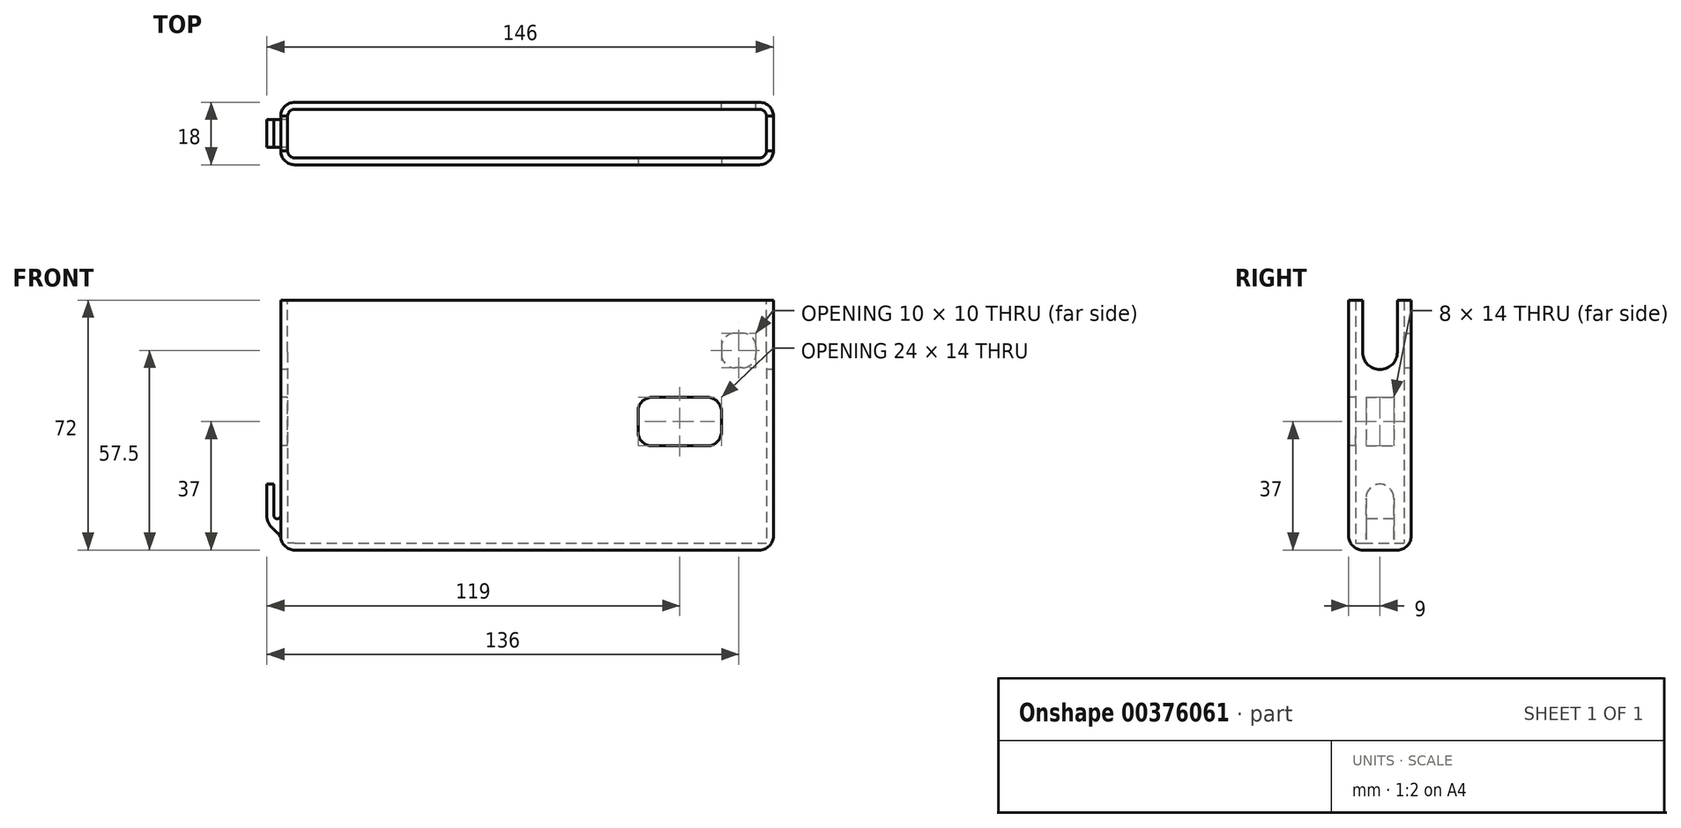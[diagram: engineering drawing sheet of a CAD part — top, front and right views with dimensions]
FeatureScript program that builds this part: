
annotation { "Feature Type Name" : "Feature", "Feature Type Description" : "" }
export const myFeature = defineFeature(function(context is Context, id is Id, definition is map)
    precondition{}
    {
        {
            var Q0;
            Q0=qCreatedBy(makeId("Top.planeOp"),FACE);
            var sketch = newSketch(context, id + "F0", { "sketchPlane" : qUnion([Q0])});
            skLineSegment(sketch, "E0.bottom", {"start": v(0, 0) * mm, "end": v(142, 0) * mm});
            skLineSegment(sketch, "E0.top", {"start": v(0, 18) * mm, "end": v(142, 18) * mm});
            skLineSegment(sketch, "E0.left", {"start": v(0, 0) * mm, "end": v(0, 18) * mm});
            skLineSegment(sketch, "E0.right", {"start": v(142, 0) * mm, "end": v(142, 18) * mm});
            skSolve(sketch);
        }
        {
            var Q0;
            Q0=qSketchRegion(id+"F0",true);
            extrude(context, id + "F1", {"entities" : qUnion([Q0]), "depth" : 2 * mm});
        }
        {
            var Q0;
            Q0=makeQuery(id+"F1.opExtrude","CAP_FACE",FACE,{"disambiguationData":[OSD([sQuery(id+"F0.wireOp",EDGE,"E0.bottom"),sQuery(id+"F0.wireOp",EDGE,"E0.top"),sQuery(id+"F0.wireOp",EDGE,"E0.left"),sQuery(id+"F0.wireOp",EDGE,"E0.right")])],"isStart":false});
            var sketch = newSketch(context, id + "F2", { "sketchPlane" : qUnion([Q0])});
            skLineSegment(sketch, "E1.0", {"start": v(0, 18) * mm, "end": v(142, 18) * mm});
            skLineSegment(sketch, "E1.1", {"start": v(0, 0) * mm, "end": v(0, 18) * mm});
            skLineSegment(sketch, "E1.2", {"start": v(0, 0) * mm, "end": v(142, 0) * mm});
            skLineSegment(sketch, "E1.3", {"start": v(142, 0) * mm, "end": v(142, 18) * mm});
            skLineSegment(sketch, "E2.0", {"start": v(2, 16) * mm, "end": v(140, 16) * mm});
            skLineSegment(sketch, "E2.1", {"start": v(2, 2) * mm, "end": v(2, 16) * mm});
            skLineSegment(sketch, "E2.2", {"start": v(2, 2) * mm, "end": v(140, 2) * mm});
            skLineSegment(sketch, "E2.3", {"start": v(140, 2) * mm, "end": v(140, 16) * mm});
            skSolve(sketch);
        }
        {
            var Q0;
            Q0=qSketchRegion(id+"F2",true);
            extrude(context, id + "F3", {"entities" : qUnion([Q0]), "operationType" : NewBodyOperationType.ADD, "depth" : 70 * mm});
        }
        {
            var Q0;
            Q0=makeQuery(id+"F3.opExtrude","SWEPT_EDGE",EDGE,{"disambiguationData":[OSD([sQuery(id+"F2.wireOp",EDGE,"E2.1"),sQuery(id+"F2.wireOp",EDGE,"E2.2")])]});
            var Q1;
            Q1=makeQuery(id+"F3.opExtrude","SWEPT_EDGE",EDGE,{"disambiguationData":[OSD([sQuery(id+"F2.wireOp",EDGE,"E2.0"),sQuery(id+"F2.wireOp",EDGE,"E2.1")])]});
            var Q2;
            Q2=makeQuery(id+"F3.opExtrude","SWEPT_EDGE",EDGE,{"disambiguationData":[OSD([sQuery(id+"F2.wireOp",EDGE,"E2.0"),sQuery(id+"F2.wireOp",EDGE,"E2.3")])]});
            var Q3;
            Q3=makeQuery(id+"F3.opExtrude","SWEPT_EDGE",EDGE,{"disambiguationData":[OSD([sQuery(id+"F2.wireOp",EDGE,"E2.2"),sQuery(id+"F2.wireOp",EDGE,"E2.3")])]});
            var Q4;
            Q4=makeQuery(id+"F3.opExtrude","CAP_EDGE",EDGE,{"disambiguationData":[OSD([sQuery(id+"F2.wireOp",EDGE,"E2.2")])],"isStart":true});
            var Q5;
            Q5=makeQuery(id+"F3.opExtrude","CAP_EDGE",EDGE,{"disambiguationData":[OSD([sQuery(id+"F2.wireOp",EDGE,"E2.3")])],"isStart":true});
            var Q6;
            Q6=makeQuery(id+"F3.opExtrude","CAP_EDGE",EDGE,{"disambiguationData":[OSD([sQuery(id+"F2.wireOp",EDGE,"E2.0")])],"isStart":true});
            var Q7;
            Q7=makeQuery(id+"F3.opExtrude","CAP_EDGE",EDGE,{"disambiguationData":[OSD([sQuery(id+"F2.wireOp",EDGE,"E2.1")])],"isStart":true});
            fillet(context, id + "F4", {"entities" : qUnion([Q0, Q1, Q2, Q3, Q4, Q5, Q6, Q7]), "radius" : 2 * mm, "tangentPropagation" : true, "allowEdgeOverflow" : false});
        }
        {
            var Q0;
            Q0=makeQuery(id+"F3.boolean.opBoolean","MERGE",EDGE,{"derivedFrom":[makeQuery(id+"F1.opExtrude","SWEPT_EDGE",EDGE,{"disambiguationData":[OSD([sQuery(id+"F0.wireOp",EDGE,"E0.bottom"),sQuery(id+"F0.wireOp",EDGE,"E0.left")])]}),makeQuery(id+"F3.opExtrude","SWEPT_EDGE",EDGE,{"disambiguationData":[OSD([sQuery(id+"F2.wireOp",EDGE,"E1.1"),sQuery(id+"F2.wireOp",EDGE,"E1.2")])]})]});
            var Q1;
            Q1=makeQuery(id+"F3.boolean.opBoolean","MERGE",EDGE,{"derivedFrom":[makeQuery(id+"F1.opExtrude","SWEPT_EDGE",EDGE,{"disambiguationData":[OSD([sQuery(id+"F0.wireOp",EDGE,"E0.top"),sQuery(id+"F0.wireOp",EDGE,"E0.left")])]}),makeQuery(id+"F3.opExtrude","SWEPT_EDGE",EDGE,{"disambiguationData":[OSD([sQuery(id+"F2.wireOp",EDGE,"E1.0"),sQuery(id+"F2.wireOp",EDGE,"E1.1")])]})]});
            var Q2;
            Q2=makeQuery(id+"F3.boolean.opBoolean","MERGE",EDGE,{"derivedFrom":[makeQuery(id+"F1.opExtrude","SWEPT_EDGE",EDGE,{"disambiguationData":[OSD([sQuery(id+"F0.wireOp",EDGE,"E0.top"),sQuery(id+"F0.wireOp",EDGE,"E0.right")])]}),makeQuery(id+"F3.opExtrude","SWEPT_EDGE",EDGE,{"disambiguationData":[OSD([sQuery(id+"F2.wireOp",EDGE,"E1.0"),sQuery(id+"F2.wireOp",EDGE,"E1.3")])]})]});
            var Q3;
            Q3=makeQuery(id+"F3.boolean.opBoolean","MERGE",EDGE,{"derivedFrom":[makeQuery(id+"F1.opExtrude","SWEPT_EDGE",EDGE,{"disambiguationData":[OSD([sQuery(id+"F0.wireOp",EDGE,"E0.bottom"),sQuery(id+"F0.wireOp",EDGE,"E0.right")])]}),makeQuery(id+"F3.opExtrude","SWEPT_EDGE",EDGE,{"disambiguationData":[OSD([sQuery(id+"F2.wireOp",EDGE,"E1.2"),sQuery(id+"F2.wireOp",EDGE,"E1.3")])]})]});
            var Q4;
            Q4=makeQuery(id+"F1.opExtrude","CAP_EDGE",EDGE,{"disambiguationData":[OSD([sQuery(id+"F0.wireOp",EDGE,"E0.bottom")])],"isStart":true});
            var Q5;
            Q5=makeQuery(id+"F1.opExtrude","CAP_EDGE",EDGE,{"disambiguationData":[OSD([sQuery(id+"F0.wireOp",EDGE,"E0.left")])],"isStart":true});
            var Q6;
            Q6=makeQuery(id+"F1.opExtrude","CAP_EDGE",EDGE,{"disambiguationData":[OSD([sQuery(id+"F0.wireOp",EDGE,"E0.top")])],"isStart":true});
            var Q7;
            Q7=makeQuery(id+"F1.opExtrude","CAP_EDGE",EDGE,{"disambiguationData":[OSD([sQuery(id+"F0.wireOp",EDGE,"E0.right")])],"isStart":true});
            fillet(context, id + "F5", {"entities" : qUnion([Q0, Q1, Q2, Q3, Q4, Q5, Q6, Q7]), "radius" : 4 * mm, "tangentPropagation" : true, "allowEdgeOverflow" : false});
        }
        {
            var Q0;
            Q0=makeQuery(id+"F3.boolean.opBoolean","MERGE",FACE,{"derivedFrom":[makeQuery(id+"F1.opExtrude","SWEPT_FACE",FACE,{"disambiguationData":[OSD([sQuery(id+"F0.wireOp",EDGE,"E0.left")])]}),makeQuery(id+"F3.opExtrude","SWEPT_FACE",FACE,{"disambiguationData":[OSD([sQuery(id+"F2.wireOp",EDGE,"E1.1")])]})]});
            var sketch = newSketch(context, id + "F6", { "sketchPlane" : qUnion([Q0])});
            skLineSegment(sketch, "E3", {"start": v(-9, 72) * mm, "end": v(-9, 57) * mm, "construction": true});
            skArc(sketch, "E4.0.startCap", {"start": v(-14, 72) * mm, "mid": v(-9, 77) * mm, "end": v(-4, 72) * mm});
            skArc(sketch, "E4.0.endCap", {"start": v(-4, 57) * mm, "mid": v(-9, 52) * mm, "end": v(-14, 57) * mm});
            skLineSegment(sketch, "E4.0.left", {"start": v(-4, 72) * mm, "end": v(-4, 57) * mm});
            skLineSegment(sketch, "E4.0.right", {"start": v(-14, 72) * mm, "end": v(-14, 57) * mm});
            skSolve(sketch);
        }
        {
            var Q0;
            Q0=qSketchRegion(id+"F6",true);
            extrude(context, id + "F7", {"entities" : qUnion([Q0]), "operationType" : NewBodyOperationType.REMOVE, "endBound" : BoundingType.THROUGH_ALL, "oppositeDirection" : true, "depth" : 25 * mm});
        }
        {
            var Q0;
            Q0=makeQuery(id+"F3.boolean.opBoolean","MERGE",FACE,{"derivedFrom":[makeQuery(id+"F1.opExtrude","SWEPT_FACE",FACE,{"disambiguationData":[OSD([sQuery(id+"F0.wireOp",EDGE,"E0.bottom")])]}),makeQuery(id+"F3.opExtrude","SWEPT_FACE",FACE,{"disambiguationData":[OSD([sQuery(id+"F2.wireOp",EDGE,"E1.2")])]})]});
            var sketch = newSketch(context, id + "F8", { "sketchPlane" : qUnion([Q0])});
            skLineSegment(sketch, "E5.bottom", {"start": v(107, 44) * mm, "end": v(123, 44) * mm});
            skLineSegment(sketch, "E5.top", {"start": v(107, 30) * mm, "end": v(123, 30) * mm});
            skLineSegment(sketch, "E5.left", {"start": v(103, 40) * mm, "end": v(103, 34) * mm});
            skLineSegment(sketch, "E5.right", {"start": v(127, 40) * mm, "end": v(127, 34) * mm});
            skPoint(sketch, "E6", {"position": v(103, 37) * mm});
            skPoint(sketch, "E7.visualSharp", {"position": v(103, 44) * mm});
            skArc(sketch, "E7.filletArc", {"start": v(107, 44) * mm, "mid": v(104.17, 42.83) * mm, "end": v(103, 40) * mm});
            skPoint(sketch, "E8.visualSharp", {"position": v(127, 44) * mm});
            skArc(sketch, "E8.filletArc", {"start": v(127, 40) * mm, "mid": v(125.83, 42.83) * mm, "end": v(123, 44) * mm});
            skPoint(sketch, "E9.visualSharp", {"position": v(127, 30) * mm});
            skArc(sketch, "E9.filletArc", {"start": v(123, 30) * mm, "mid": v(125.83, 31.17) * mm, "end": v(127, 34) * mm});
            skPoint(sketch, "E10.visualSharp", {"position": v(103, 30) * mm});
            skArc(sketch, "E10.filletArc", {"start": v(103, 34) * mm, "mid": v(104.17, 31.17) * mm, "end": v(107, 30) * mm});
            skPoint(sketch, "E11", {"position": v(115, 44) * mm});
            skSolve(sketch);
        }
        {
            var Q0;
            Q0=qSketchRegion(id+"F8",true);
            extrude(context, id + "F9", {"entities" : qUnion([Q0]), "operationType" : NewBodyOperationType.REMOVE, "endBound" : BoundingType.UP_TO_NEXT, "oppositeDirection" : true, "depth" : 25 * mm});
        }
        {
            var Q0;
            Q0=makeQuery(id+"F3.boolean.opBoolean","MERGE",FACE,{"derivedFrom":[makeQuery(id+"F1.opExtrude","SWEPT_FACE",FACE,{"disambiguationData":[OSD([sQuery(id+"F0.wireOp",EDGE,"E0.left")])]}),makeQuery(id+"F3.opExtrude","SWEPT_FACE",FACE,{"disambiguationData":[OSD([sQuery(id+"F2.wireOp",EDGE,"E1.1")])]})]});
            var sketch = newSketch(context, id + "F10", { "sketchPlane" : qUnion([Q0])});
            skLineSegment(sketch, "E12.bottom", {"start": v(-13, 19) * mm, "end": v(-5, 19) * mm});
            skLineSegment(sketch, "E12.top", {"start": v(-13, 4) * mm, "end": v(-5, 4) * mm});
            skLineSegment(sketch, "E12.left", {"start": v(-13, 19) * mm, "end": v(-13, 4) * mm});
            skLineSegment(sketch, "E12.right", {"start": v(-5, 19) * mm, "end": v(-5, 4) * mm});
            skPoint(sketch, "E13", {"position": v(-9, 4) * mm});
            skSolve(sketch);
        }
        {
            var Q0;
            Q0=qSketchRegion(id+"F10",true);
            extrude(context, id + "F11", {"entities" : qUnion([Q0]), "operationType" : NewBodyOperationType.ADD, "depth" : 4 * mm});
        }
        {
            var Q0;
            Q0=makeQuery(id+"F11.opExtrude","CAP_EDGE",EDGE,{"disambiguationData":[OSD([sQuery(id+"F10.wireOp",EDGE,"E12.top")])],"isStart":false});
            chamfer(context, id + "F12", {"entities" : qUnion([Q0]), "width" : 4 * mm, "tangentPropagation" : true});
        }
        {
            var Q0;
            Q0=makeQuery(id+"F11.opExtrude","SWEPT_FACE",FACE,{"disambiguationData":[OSD([sQuery(id+"F10.wireOp",EDGE,"E12.bottom")])]});
            var sketch = newSketch(context, id + "F13", { "sketchPlane" : qUnion([Q0])});
            skLineSegment(sketch, "E14.bottom", {"start": v(-2, 13) * mm, "end": v(0, 13) * mm});
            skLineSegment(sketch, "E14.top", {"start": v(-2, 5) * mm, "end": v(0, 5) * mm});
            skLineSegment(sketch, "E14.left", {"start": v(0, 5) * mm, "end": v(0, 13) * mm});
            skLineSegment(sketch, "E14.right", {"start": v(-2, 5) * mm, "end": v(-2, 13) * mm});
            skSolve(sketch);
        }
        {
            var Q0;
            Q0=qSketchRegion(id+"F13",true);
            extrude(context, id + "F14", {"entities" : qUnion([Q0]), "operationType" : NewBodyOperationType.REMOVE, "oppositeDirection" : true, "depth" : 10 * mm});
        }
        {
            var Q0;
            Q0=makeQuery(id+"F11.opExtrude","SWEPT_EDGE",EDGE,{"disambiguationData":[OSD([sQuery(id+"F10.wireOp",EDGE,"E12.bottom"),sQuery(id+"F10.wireOp",EDGE,"E12.left")])]});
            var Q1;
            Q1=makeQuery(id+"F11.opExtrude","SWEPT_EDGE",EDGE,{"disambiguationData":[OSD([sQuery(id+"F10.wireOp",EDGE,"E12.bottom"),sQuery(id+"F10.wireOp",EDGE,"E12.right")])]});
            var Q2;
            {var subQ0=sQuery(id+"F10.wireOp",EDGE,"E12.top");Q2=makeQuery(id+"F12.opChamfer","BLEND_EDGE",EDGE,{"blendedFrom":[makeQuery(id+"F11.opExtrude","CAP_EDGE",EDGE,{"disambiguationData":[OSD([subQ0])],"isStart":false}),makeQuery(id+"F11.opExtrude","CAP_FACE",FACE,{"disambiguationData":[OSD([sQuery(id+"F10.wireOp",EDGE,"E12.bottom"),subQ0,sQuery(id+"F10.wireOp",EDGE,"E12.left"),sQuery(id+"F10.wireOp",EDGE,"E12.right")])],"isStart":false})],"blendedInto":[makeQuery(id+"F11.opExtrude","CAP_FACE",FACE,{"disambiguationData":[OSD([sQuery(id+"F10.wireOp",EDGE,"E12.bottom"),subQ0,sQuery(id+"F10.wireOp",EDGE,"E12.left"),sQuery(id+"F10.wireOp",EDGE,"E12.right")])],"isStart":false})]});}
            var Q3;
            Q3=makeQuery(id+"F12.opChamfer","BLEND_EDGE",EDGE,{"blendedFrom":[makeQuery(id+"F11.opExtrude","CAP_EDGE",EDGE,{"disambiguationData":[OSD([sQuery(id+"F10.wireOp",EDGE,"E12.top")])],"isStart":false}),makeQuery(id+"F5.opFillet","BLEND_FACE",FACE,{"disambiguationData":[OSD([sQuery(id+"F0.wireOp",EDGE,"E0.right")])]})],"blendedInto":[makeQuery(id+"F5.opFillet","BLEND_FACE",FACE,{"disambiguationData":[OSD([sQuery(id+"F0.wireOp",EDGE,"E0.right")])]})]});
            var Q4;
            Q4=makeQuery(id+"F12.opChamfer","BLEND_EDGE",EDGE,{"blendedFrom":[makeQuery(id+"F11.opExtrude","CAP_EDGE",EDGE,{"disambiguationData":[OSD([sQuery(id+"F10.wireOp",EDGE,"E12.top")])],"isStart":false}),makeQuery(id+"F5.opFillet","BLEND_FACE",FACE,{"disambiguationData":[OSD([sQuery(id+"F0.wireOp",EDGE,"E0.left")])]})],"blendedInto":[makeQuery(id+"F5.opFillet","BLEND_FACE",FACE,{"disambiguationData":[OSD([sQuery(id+"F0.wireOp",EDGE,"E0.left")])]})]});
            fillet(context, id + "F15", {"entities" : qUnion([Q0, Q1, Q2, Q3, Q4]), "radius" : 4 * mm, "tangentPropagation" : true, "allowEdgeOverflow" : false});
        }
        {
            var Q0;
            Q0=makeQuery(id+"F14.boolean.opBoolean","COPY",EDGE,{"derivedFrom":makeQuery(id+"F14.opExtrude","CAP_EDGE",EDGE,{"disambiguationData":[OSD([sQuery(id+"F13.wireOp",EDGE,"E14.right")])],"isStart":false})});
            var Q1;
            Q1=makeQuery(id+"F14.boolean.opBoolean","COPY",EDGE,{"derivedFrom":makeQuery(id+"F14.opExtrude","CAP_EDGE",EDGE,{"disambiguationData":[OSD([sQuery(id+"F13.wireOp",EDGE,"E14.left")])],"isStart":false})});
            fillet(context, id + "F16", {"entities" : qUnion([Q0, Q1]), "radius" : 1 * mm, "tangentPropagation" : true, "allowEdgeOverflow" : false});
        }
        {
            var Q0;
            Q0=makeQuery(id+"F3.boolean.opBoolean","MERGE",FACE,{"derivedFrom":[makeQuery(id+"F1.opExtrude","SWEPT_FACE",FACE,{"disambiguationData":[OSD([sQuery(id+"F0.wireOp",EDGE,"E0.top")])]}),makeQuery(id+"F3.opExtrude","SWEPT_FACE",FACE,{"disambiguationData":[OSD([sQuery(id+"F2.wireOp",EDGE,"E1.0")])]})]});
            var sketch = newSketch(context, id + "F17", { "sketchPlane" : qUnion([Q0])});
            skLineSegment(sketch, "E15.bottom", {"start": v(-133, 62.5) * mm, "end": v(-131, 62.5) * mm});
            skLineSegment(sketch, "E15.top", {"start": v(-133, 52.5) * mm, "end": v(-131, 52.5) * mm});
            skLineSegment(sketch, "E15.left", {"start": v(-137, 58.5) * mm, "end": v(-137, 56.5) * mm});
            skLineSegment(sketch, "E15.right", {"start": v(-127, 58.5) * mm, "end": v(-127, 56.5) * mm});
            skPoint(sketch, "E16.visualSharp", {"position": v(-137, 62.5) * mm});
            skArc(sketch, "E16.filletArc", {"start": v(-133, 62.5) * mm, "mid": v(-135.83, 61.33) * mm, "end": v(-137, 58.5) * mm});
            skPoint(sketch, "E17.visualSharp", {"position": v(-127, 62.5) * mm});
            skArc(sketch, "E17.filletArc", {"start": v(-127, 58.5) * mm, "mid": v(-128.17, 61.33) * mm, "end": v(-131, 62.5) * mm});
            skPoint(sketch, "E18.visualSharp", {"position": v(-127, 52.5) * mm});
            skArc(sketch, "E18.filletArc", {"start": v(-131, 52.5) * mm, "mid": v(-128.17, 53.67) * mm, "end": v(-127, 56.5) * mm});
            skPoint(sketch, "E19.visualSharp", {"position": v(-137, 52.5) * mm});
            skArc(sketch, "E19.filletArc", {"start": v(-137, 56.5) * mm, "mid": v(-135.83, 53.67) * mm, "end": v(-133, 52.5) * mm});
            skPoint(sketch, "E20", {"position": v(-132, 62.5) * mm});
            skPoint(sketch, "E21", {"position": v(-127, 57.5) * mm});
            skSolve(sketch);
        }
        {
            var Q0;
            Q0 = qSketchRegion(id + "F17", true);
            extrude(context, id + "F18", {"entities" : qUnion([Q0]), "operationType" : NewBodyOperationType.REMOVE, "endBound" : BoundingType.UP_TO_NEXT, "oppositeDirection" : true, "depth" : 25 * mm});
        }
        {
            var Q0;
            Q0=makeQuery(id+"F3.boolean.opBoolean","MERGE",FACE,{"derivedFrom":[makeQuery(id+"F1.opExtrude","SWEPT_FACE",FACE,{"disambiguationData":[OSD([sQuery(id+"F0.wireOp",EDGE,"E0.left")])]}),makeQuery(id+"F3.opExtrude","SWEPT_FACE",FACE,{"disambiguationData":[OSD([sQuery(id+"F2.wireOp",EDGE,"E1.1")])]})]});
            var sketch = newSketch(context, id + "F19", { "sketchPlane" : qUnion([Q0])});
            skLineSegment(sketch, "E22.bottom", {"start": v(-5, 44) * mm, "end": v(-13, 44) * mm});
            skLineSegment(sketch, "E22.top", {"start": v(-5, 30) * mm, "end": v(-13, 30) * mm});
            skLineSegment(sketch, "E22.left", {"start": v(-5, 44) * mm, "end": v(-5, 30) * mm});
            skLineSegment(sketch, "E22.right", {"start": v(-13, 44) * mm, "end": v(-13, 30) * mm});
            skPoint(sketch, "E22.middle", {"position": v(-9, 37) * mm});
            skLineSegment(sketch, "E23", {"start": v(-14, 30.5) * mm, "end": v(-4, 30.5) * mm, "construction": true});
            skPoint(sketch, "E24", {"position": v(-9, 30.5) * mm});
            skSolve(sketch);
        }
        {
            var Q0;
            Q0 = qSketchRegion(id + "F19", true);
            extrude(context, id + "F20", {"entities" : qUnion([Q0]), "operationType" : NewBodyOperationType.REMOVE, "endBound" : BoundingType.UP_TO_NEXT, "oppositeDirection" : true, "depth" : 25 * mm});
        }
    });
